# Revit family: IS_Tempo_Multiproduct_BIM_DE_E3240;E3242
name_source: partatom
category: Plumbing Fixtures
revit_build: Autodesk Revit MEP 2016 (Build: 20161004_0715(x64)
units: mm (PartAtom-declared; Revit-internal decimal feet)

## family parameters
Cut with Voids When Loaded = No
Host = Face
OmniClass Number = 23.45.05.14.21.11
OmniClass Title = Bath/Shower Units
Part Type = Normal
Room Calculation Point = No
Round Connector Dimension = Use Diameter
Shared = Yes

## types (4) — shared parameters
Accessories = www.idealspec.co.uk
AreaUnits = millimeters
Assembly Code = C1030200
AssetType = Fixed
BIMObjectName = -2146826246
Brand = Ideal Standard
ChromeHandle = IS_IdealStandard_Fitting_Chrome_Render
CodePerformance = 0
ConnectionType = Mechanical
CurrencyUnit = €
Default Elevation = 900 mm  [stored 2.95276 ft]
DurationUnit = year
ExpectedLife = 25
IfcExportAs = IfcFurnitureType
InstallationInstructions = www.idealstandard.de\produkte
LinearUnits = millimeters
ManufacturerURL = www.idealstandard.de
NBSDescription = Bathroom integrated duct work
NBSReference = 45-35-72/320
Name = -2146826246
NominalDepth = 440 mm
NominalHeight = 500 mm
NominalLength = 500 mm
ProductInformation = www.idealstandard.de
Shape = Rectangular
Space = Internal
SpareParts = www.idealstandard.de/ersatzteile
URL = www.idealstandard.de
Uniclass2015Code = Pr_40_30_78_05
Uniclass2015Title = Bathroom furniture
Uniclass2015Version = Products v1.1
Version = 1
VolumeUnits = Litres
zero-valued in all types: Cost

## per-type parameters (varying)
| type | BarCode | Color | Description | Features | Finish | GrossWeight | HandleDistance | LaminateFinish | Model | ModelNumber | ModelReference | NettWeight | NominalWidth | Size |
| E3240SG - Tempo 600mm Wall-mounted Vanity Basin Unit - Two Drawers - Sandy Grey | 5017830475644 | Sandy Grey | Tempo 600mm wall mounted vanity basin unit  two drawers | EUROVIT vanity unit 610x450mm, 2 drawer | Sandy Grey | 22,743 kg | 150 mm | IS_IdealStandard_Laminate_SandyGrey_SG_Render | E3240SG | E3240SG | Tempo 600mm wall mounted vanity basin unit  two drawers | 19,95 kg | 600 mm | 440 x 500 x 600 mm |
| E3242SG - Tempo 800mm Wall-mounted Vanity Basin Unit - Two Drawers - Sandy Grey | 5017830475705 | Sandy Grey | Tempo 800mm wall mounted vanity basin unit  two drawers | EUROVIT vanity unit 815x450mm, 2 drawer | Sandy Grey | 26,562 kg | 250 mm  [stored 0.82021 ft] | IS_IdealStandard_Laminate_SandyGrey_SG_Render | E3242SG | E3242SG | Tempo 800mm wall mounted vanity basin unit  two drawers | 23,3 kg | 800 mm  [stored 2.62467 ft] | 440 x 500 x 800 mm |
| E3240WG - Tempo 600mm Wall-mounted Vanity Basin Unit - Two Drawers – White Gloss | 5017830475651 | Glossy White | Tempo 600mm wall mounted vanity basin unit  two drawers | EUROVIT vanity unit 610x450mm, 2 drawer | Glossy White | 22,743 kg | 150 mm | IS_IdealStandard_Laminate_White_WG_Render | E3240WG | E3240WG | Tempo 600mm wall mounted vanity basin unit  two drawers | 19,95 kg | 600 mm | 440 x 500 x 600 mm |
| E3242WG - Tempo 800mm Wall-mounted Vanity Basin Unit - Two Drawers – White Gloss | 5017830475712 | Glossy White | Tempo 800mm wall mounted vanity basin unit  two drawers | EUROVIT vanity unit 815x450mm, 2 drawer | Glossy White | 26,562 kg | 250 mm  [stored 0.82021 ft] | IS_IdealStandard_Laminate_White_WG_Render | E3242WG | E3242WG | Tempo 800mm wall mounted vanity basin unit  two drawers | 23,3 kg | 800 mm  [stored 2.62467 ft] | 440 x 500 x 800 mm |

note: [stored X ft] marks values corroborated as IEEE doubles in the binary element streams (Revit-internal decimal feet)

## geometry (parser evidence)
native form markers: Blend x2, Sweep x3
no freeform markers — native parametric forms only
